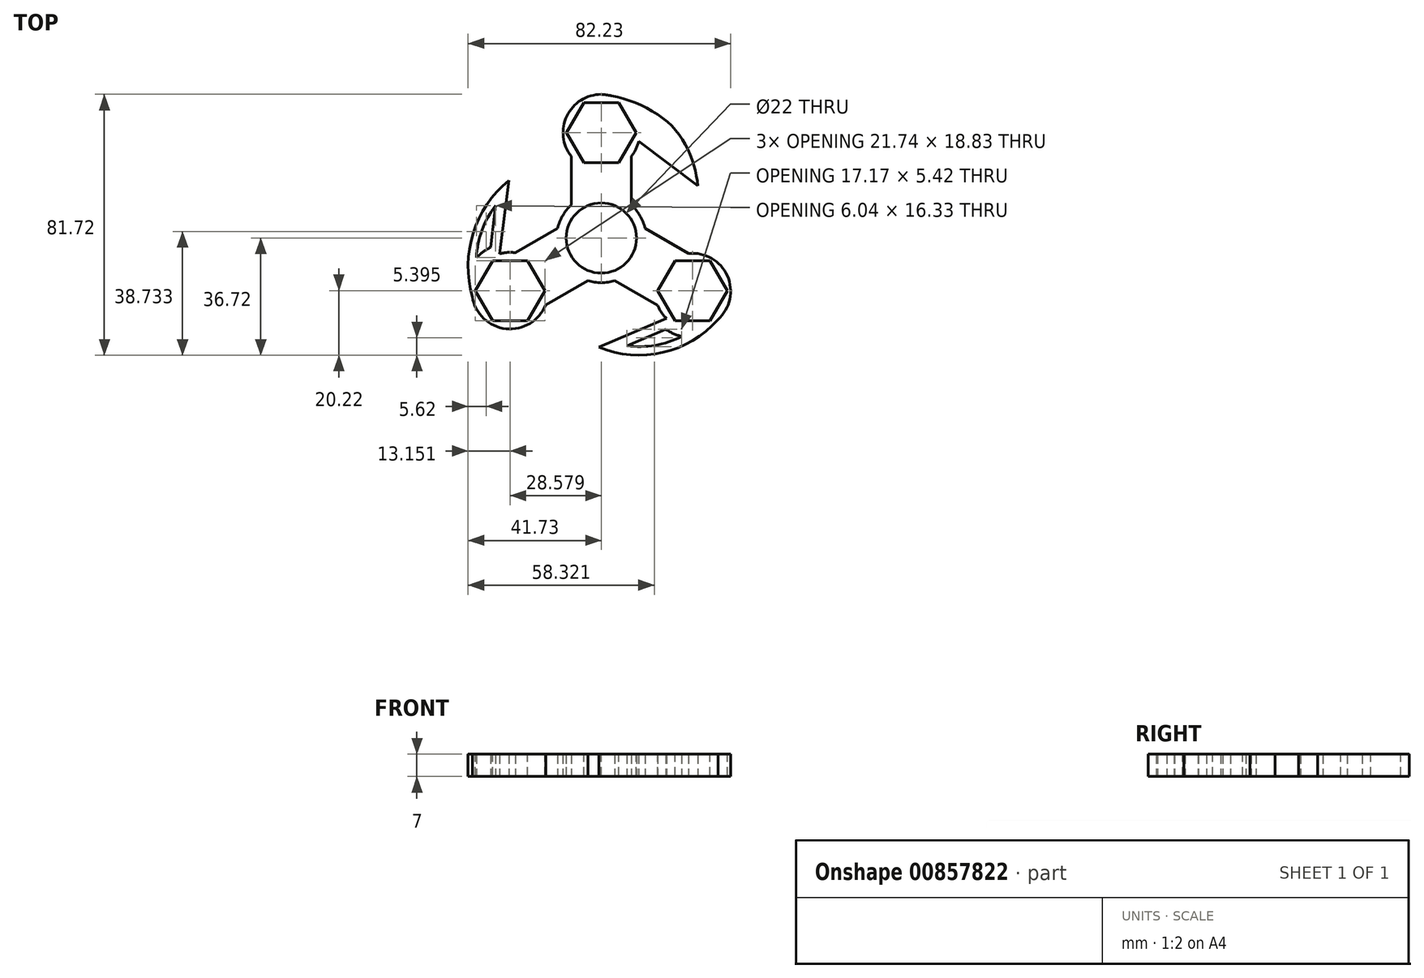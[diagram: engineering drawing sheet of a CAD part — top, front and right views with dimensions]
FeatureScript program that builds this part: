
annotation { "Feature Type Name" : "Feature", "Feature Type Description" : "" }
export const myFeature = defineFeature(function(context is Context, id is Id, definition is map)
    precondition{}
    {
        {
            var Q0;
            Q0=qCreatedBy(makeId("Top.planeOp"),FACE);
            var sketch = newSketch(context, id + "F0", { "sketchPlane" : qUnion([Q0])});
            skCircle(sketch, "E0", {"center": v(0, 0) * mm, "radius": 45 * mm, "construction": true});
            skCircle(sketch, "E1", {"center": v(0, 0) * mm, "radius": 11 * mm});
            skArc(sketch, "E2.0", {"start": v(-4.24, -13.34) * mm, "mid": v(0, -14) * mm, "end": v(4.24, -13.34) * mm});
            skArc(sketch, "E3", {"start": v(9.43, 25.58) * mm, "mid": v(10.84, 27.85) * mm, "end": v(11.7, 30.37) * mm});
            skLineSegment(sketch, "E4", {"start": v(-9.43, 10.35) * mm, "end": v(-9.43, 25.58) * mm});
            skLineSegment(sketch, "E5", {"start": v(9.43, 25.58) * mm, "end": v(9.43, 10.35) * mm});
            skLineSegment(sketch, "E6", {"start": v(34.52, 28.87) * mm, "end": v(34.52, 28.87) * mm});
            skArc(sketch, "E7.1.0", {"start": v(-40.41, -18.5) * mm, "mid": v(-29.86, -28.43) * mm, "end": v(-17.44, -20.96) * mm});
            skArc(sketch, "E7.2.0", {"start": v(17.63, -21.07) * mm, "mid": v(18.79, -23.28) * mm, "end": v(20.39, -25.2) * mm});
            skLineSegment(sketch, "E8.1.0", {"start": v(-4.24, -13.34) * mm, "end": v(-17.44, -20.96) * mm});
            skLineSegment(sketch, "E8.1.1", {"start": v(-26.87, -4.62) * mm, "end": v(-13.68, 3) * mm});
            skLineSegment(sketch, "E8.2.0", {"start": v(13.68, 3) * mm, "end": v(27.33, -4.89) * mm});
            skLineSegment(sketch, "E8.2.1", {"start": v(17.63, -21.07) * mm, "end": v(4.24, -13.34) * mm});
            skLineSegment(sketch, "E9", {"start": v(30.26, 16.34) * mm, "end": v(11.7, 30.37) * mm});
            skFitSpline(sketch, "E10", {"points": [v(0, 45) * mm, v(22.31, 34.82) * mm, v(30.26, 16.34) * mm], "startDerivative": vector(43.2, -3.65) * mm, "endDerivative": vector(4.48, -39.27) * mm});
            skFitSpline(sketch, "E11.0", {"points": [v(-0.25, 42.01) * mm, v(1.36, 41.87) * mm, v(4.83, 41.28) * mm, v(10.2, 39.47) * mm, v(14.45, 37.28) * mm, v(17.46, 35.19) * mm, v(19.48, 33.47) * mm, v(21.2, 31.63) * mm, v(22.69, 29.64) * mm, v(23.94, 27.51) * mm, v(25.34, 24.55) * mm, v(26.58, 20.66) * mm, v(27.1, 17.52) * mm, v(27.28, 16) * mm]});
            skLineSegment(sketch, "E12.trimOffspring", {"start": v(25.53, 23.8) * mm, "end": v(14.95, 31.79) * mm});
            skArc(sketch, "E13.0", {"start": v(14.95, 31.79) * mm, "mid": v(14.92, 34.52) * mm, "end": v(14.4, 37.2) * mm});
            skLineSegment(sketch, "E14.1.0", {"start": v(-33.09, 10.18) * mm, "end": v(-34.72, -2.98) * mm});
            skArc(sketch, "E14.1.1", {"start": v(-34.72, -2.98) * mm, "mid": v(-37.07, -4.36) * mm, "end": v(-39.13, -6.15) * mm});
            skLineSegment(sketch, "E14.1.2", {"start": v(-29, 18) * mm, "end": v(-31.86, -4.96) * mm});
            skLineSegment(sketch, "E14.2.0", {"start": v(8, -33.78) * mm, "end": v(20.22, -28.61) * mm});
            skArc(sketch, "E14.2.1", {"start": v(20.22, -28.61) * mm, "mid": v(22.6, -29.95) * mm, "end": v(25.18, -30.84) * mm});
            skLineSegment(sketch, "E14.2.2", {"start": v(-0.81, -34.15) * mm, "end": v(20.39, -25.2) * mm});
            skPoint(sketch, "E14.center", {"position": v(0.15, 0.07) * mm});
            skArc(sketch, "E15", {"start": v(-33.09, 10.18) * mm, "mid": v(-37.36, 2.47) * mm, "end": v(-39.13, -6.15) * mm});
            skArc(sketch, "E16", {"start": v(8, -33.78) * mm, "mid": v(16.82, -33.62) * mm, "end": v(25.18, -30.84) * mm});
            skArc(sketch, "E17", {"start": v(-29, 18) * mm, "mid": v(-40.14, 1.45) * mm, "end": v(-40.41, -18.5) * mm});
            skArc(sketch, "E18", {"start": v(-0.81, -34.15) * mm, "mid": v(19.24, -35.88) * mm, "end": v(36.52, -25.54) * mm});
            skArc(sketch, "E19.trimOffspring", {"start": v(-39.13, -22.22) * mm, "mid": v(-39.12, -22.23) * mm, "end": v(-39.12, -22.24) * mm});
            skArc(sketch, "E20.trimOffspring", {"start": v(-26.87, -4.62) * mm, "mid": v(-29.38, -4.53) * mm, "end": v(-31.86, -4.96) * mm});
            skArc(sketch, "E21.trimOffspring", {"start": v(13.68, 3) * mm, "mid": v(12.12, 7) * mm, "end": v(9.43, 10.35) * mm});
            skArc(sketch, "E22.trimOffspring", {"start": v(-9.43, 10.35) * mm, "mid": v(-12.12, 7) * mm, "end": v(-13.68, 3) * mm});
            skArc(sketch, "E23.trimOffspring", {"start": v(3.23, 44.56) * mm, "mid": v(-9.98, 39.66) * mm, "end": v(-9.43, 25.58) * mm});
            skArc(sketch, "E24.trimOffspring", {"start": v(36.52, -25.54) * mm, "mid": v(39.48, -11.86) * mm, "end": v(27.33, -4.89) * mm});
            skSolve(sketch);
        }
        {
            var Q0;
            Q0=makeQuery(id+"F0.imprint","IMPRINT",FACE,{"disambiguationData":[TD([[makeQuery(id+"F0.imprint","IMPRINT",EDGE,{"derivedFrom":sQuery(id+"F0.wireOp",EDGE,"E1")}),-1.0]])]});
            extrude(context, id + "F1", {"entities" : qUnion([Q0]), "depth" : 7 * mm, "offsetDistance" : 25 * mm});
        }
        {
            var Q0;
            Q0=makeQuery(id+"F1.opExtrude","CAP_FACE",FACE,{"disambiguationData":[OSD([sQuery(id+"F0.wireOp",EDGE,"E1"),sQuery(id+"F0.wireOp",EDGE,"E2.0"),sQuery(id+"F0.wireOp",EDGE,"E3"),sQuery(id+"F0.wireOp",EDGE,"E4"),sQuery(id+"F0.wireOp",EDGE,"E5"),sQuery(id+"F0.wireOp",EDGE,"E7.1.0"),sQuery(id+"F0.wireOp",EDGE,"E7.2.0"),sQuery(id+"F0.wireOp",EDGE,"E8.1.0"),sQuery(id+"F0.wireOp",EDGE,"E8.1.1"),sQuery(id+"F0.wireOp",EDGE,"E8.2.0"),sQuery(id+"F0.wireOp",EDGE,"E8.2.1"),sQuery(id+"F0.wireOp",EDGE,"E9"),sQuery(id+"F0.wireOp",EDGE,"E10"),sQuery(id+"F0.wireOp",EDGE,"E11.0"),sQuery(id+"F0.wireOp",EDGE,"E12.trimOffspring"),sQuery(id+"F0.wireOp",EDGE,"E13.0"),sQuery(id+"F0.wireOp",EDGE,"E14.1.0"),sQuery(id+"F0.wireOp",EDGE,"E14.1.1"),sQuery(id+"F0.wireOp",EDGE,"E14.1.2"),sQuery(id+"F0.wireOp",EDGE,"E14.2.0"),sQuery(id+"F0.wireOp",EDGE,"E14.2.1"),sQuery(id+"F0.wireOp",EDGE,"E14.2.2"),sQuery(id+"F0.wireOp",EDGE,"E15"),sQuery(id+"F0.wireOp",EDGE,"E16"),sQuery(id+"F0.wireOp",EDGE,"E17"),sQuery(id+"F0.wireOp",EDGE,"E18"),sQuery(id+"F0.wireOp",EDGE,"E20.trimOffspring"),sQuery(id+"F0.wireOp",EDGE,"E21.trimOffspring"),sQuery(id+"F0.wireOp",EDGE,"E22.trimOffspring"),sQuery(id+"F0.wireOp",EDGE,"E23.trimOffspring"),sQuery(id+"F0.wireOp",EDGE,"E24.trimOffspring")])],"isStart":false});
            var sketch = newSketch(context, id + "F2", { "sketchPlane" : qUnion([Q0])});
            skCircle(sketch, "E25.cCircle", {"center": v(0, 33) * mm, "radius": 9.41 * mm, "construction": true});
            skLineSegment(sketch, "E25.0", {"start": v(5.44, 23.59) * mm, "end": v(-5.44, 23.59) * mm});
            skLineSegment(sketch, "E25.1", {"start": v(-5.44, 23.59) * mm, "end": v(-10.87, 33) * mm});
            skLineSegment(sketch, "E25.2", {"start": v(-10.87, 33) * mm, "end": v(-5.44, 42.41) * mm});
            skLineSegment(sketch, "E25.3", {"start": v(-5.44, 42.42) * mm, "end": v(5.44, 42.42) * mm});
            skLineSegment(sketch, "E25.4", {"start": v(5.44, 42.41) * mm, "end": v(10.87, 33) * mm});
            skLineSegment(sketch, "E25.5", {"start": v(10.87, 33) * mm, "end": v(5.44, 23.59) * mm});
            skPoint(sketch, "E25.0.midPoint", {"position": v(0, 23.59) * mm});
            skLineSegment(sketch, "E26.1.0", {"start": v(-17.7, -16.5) * mm, "end": v(-23.14, -25.91) * mm});
            skLineSegment(sketch, "E26.1.1", {"start": v(-23.14, -25.91) * mm, "end": v(-34.01, -25.91) * mm});
            skLineSegment(sketch, "E26.1.2", {"start": v(-34.01, -25.91) * mm, "end": v(-39.45, -16.5) * mm});
            skLineSegment(sketch, "E26.1.3", {"start": v(-39.45, -16.5) * mm, "end": v(-34.01, -7.08) * mm});
            skLineSegment(sketch, "E26.1.4", {"start": v(-34.01, -7.08) * mm, "end": v(-23.14, -7.09) * mm});
            skLineSegment(sketch, "E26.1.5", {"start": v(-23.14, -7.08) * mm, "end": v(-17.7, -16.5) * mm});
            skLineSegment(sketch, "E26.2.0", {"start": v(23.14, -7.09) * mm, "end": v(34.01, -7.09) * mm});
            skLineSegment(sketch, "E26.2.1", {"start": v(34.01, -7.09) * mm, "end": v(39.45, -16.5) * mm});
            skLineSegment(sketch, "E26.2.2", {"start": v(39.45, -16.5) * mm, "end": v(34.01, -25.92) * mm});
            skLineSegment(sketch, "E26.2.3", {"start": v(34.01, -25.92) * mm, "end": v(23.14, -25.92) * mm});
            skLineSegment(sketch, "E26.2.4", {"start": v(23.14, -25.92) * mm, "end": v(17.7, -16.5) * mm});
            skLineSegment(sketch, "E26.2.5", {"start": v(17.7, -16.5) * mm, "end": v(23.14, -7.09) * mm});
            skPoint(sketch, "E26.center", {"position": v(0, 0) * mm});
            skSolve(sketch);
        }
        {
            var Q0;
            Q0 = qSketchRegion(id + "F2", true);
            extrude(context, id + "F3", {"entities" : qUnion([Q0]), "operationType" : NewBodyOperationType.REMOVE, "oppositeDirection" : true, "depth" : 7 * mm, "offsetDistance" : 25 * mm});
        }
    });
